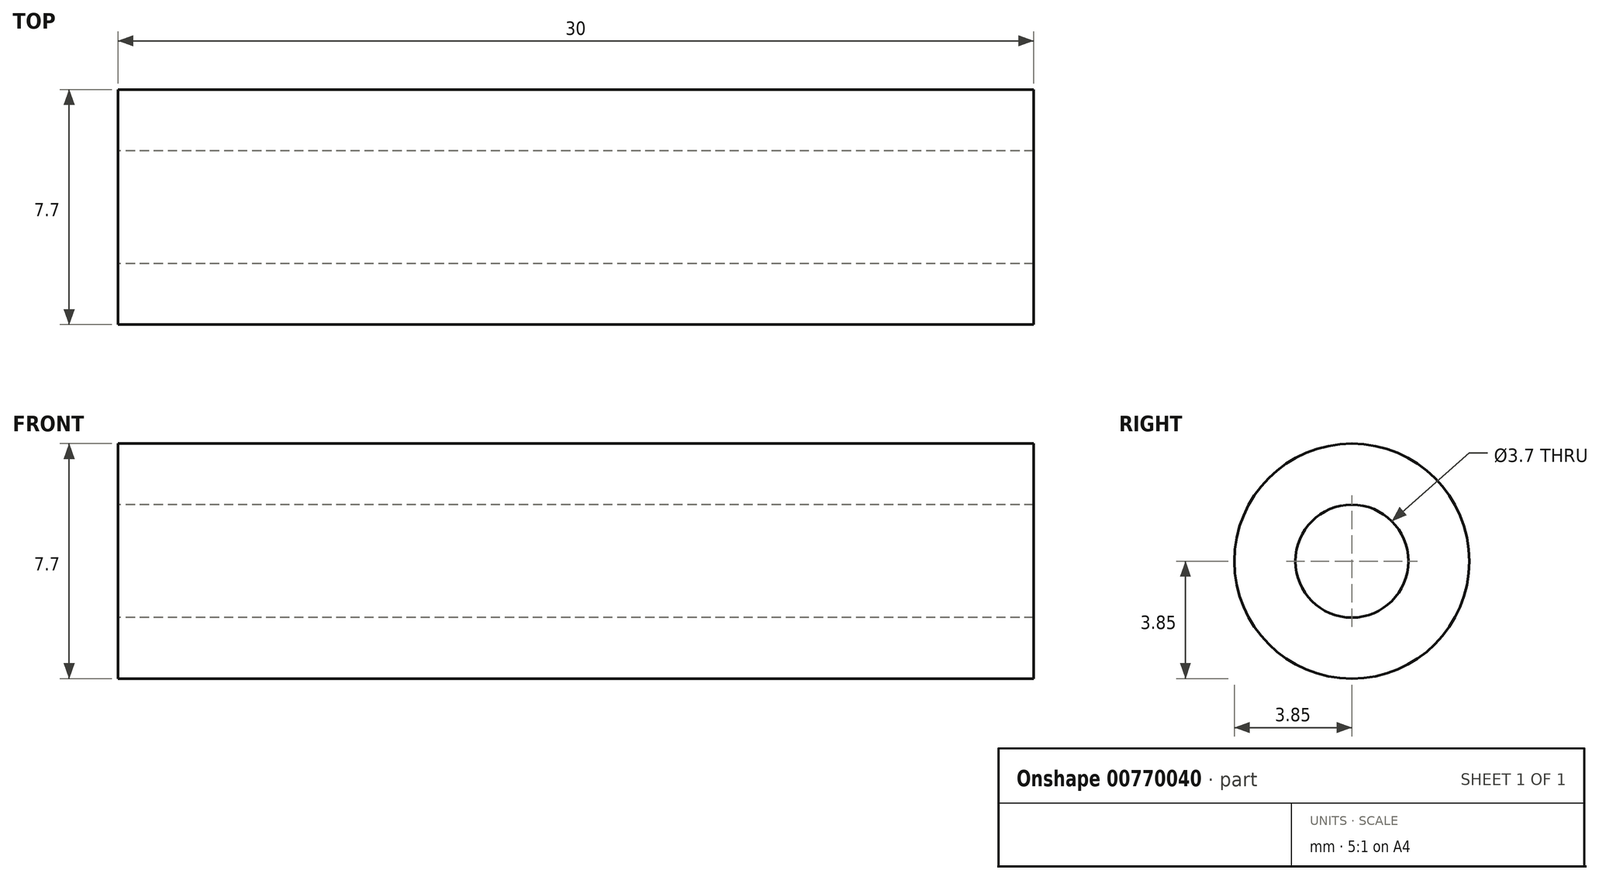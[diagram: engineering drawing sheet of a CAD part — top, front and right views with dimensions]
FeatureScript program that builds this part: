
annotation { "Feature Type Name" : "Feature", "Feature Type Description" : "" }
export const myFeature = defineFeature(function(context is Context, id is Id, definition is map)
    precondition{}
    {
        {
            var Q0;
            Q0=qCreatedBy(makeId("Right.planeOp"),FACE);
            var sketch = newSketch(context, id + "F0", { "sketchPlane" : qUnion([Q0])});
            skCircle(sketch, "E0", {"center": v(0, 0) * mm, "radius": 3.85 * mm});
            skCircle(sketch, "E1", {"center": v(0, 0) * mm, "radius": 1.85 * mm});
            skSolve(sketch);
        }
        {
            var Q0;
            Q0=makeQuery(id+"F0.imprint","IMPRINT",FACE,{"disambiguationData":[TD([[makeQuery(id+"F0.imprint","IMPRINT",EDGE,{"derivedFrom":sQuery(id+"F0.wireOp",EDGE,"E0")}),1.0]])]});
            extrude(context, id + "F1", {"entities" : qUnion([Q0]), "endBound" : BoundingType.SYMMETRIC, "depth" : 30 * mm, "offsetDistance" : 25.4 * mm});
        }
    });
